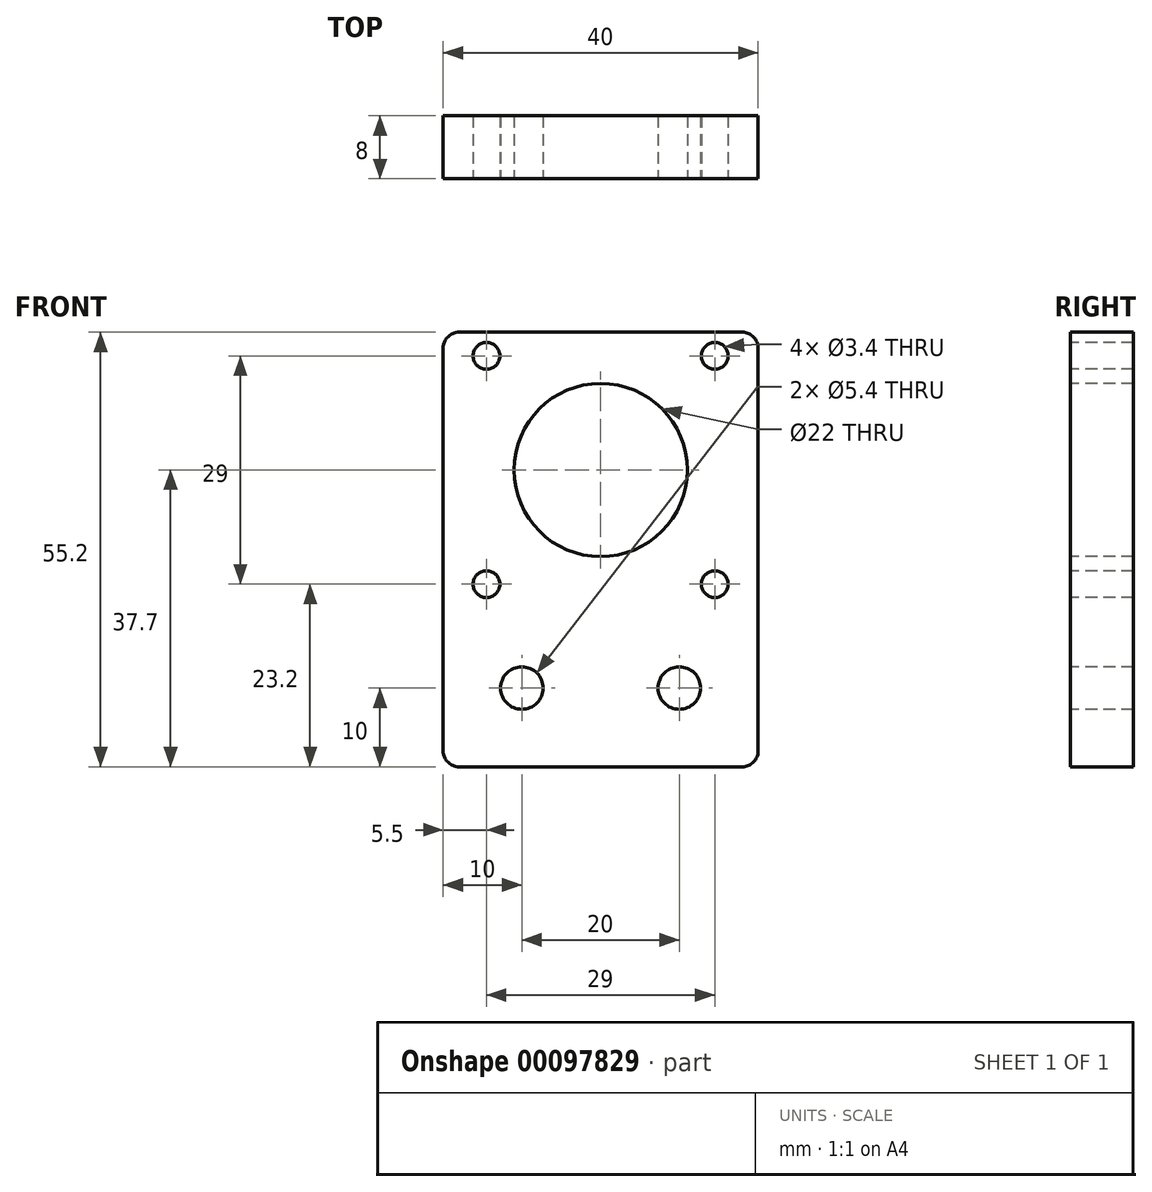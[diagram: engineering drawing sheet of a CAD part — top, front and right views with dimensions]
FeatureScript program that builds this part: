
annotation { "Feature Type Name" : "Feature", "Feature Type Description" : "" }
export const myFeature = defineFeature(function(context is Context, id is Id, definition is map)
    precondition{}
    {
        {
            var Q0;
            Q0=qCreatedBy(makeId("Front.planeOp"),FACE);
            var sketch = newSketch(context, id + "F0", { "sketchPlane" : qUnion([Q0])});
            skLineSegment(sketch, "E0.bottom", {"start": v(20, -17.5) * mm, "end": v(-20, -17.5) * mm, "construction": true});
            skLineSegment(sketch, "E0.top", {"start": v(20, 17.5) * mm, "end": v(-20, 17.5) * mm, "construction": true});
            skLineSegment(sketch, "E0.left", {"start": v(20, -17.5) * mm, "end": v(20, 17.5) * mm, "construction": true});
            skLineSegment(sketch, "E0.right", {"start": v(-20, -17.5) * mm, "end": v(-20, 17.5) * mm, "construction": true});
            skPoint(sketch, "E0.middle", {"position": v(0, 0) * mm});
            skLineSegment(sketch, "E1.bottom", {"start": v(14.5, -14.5) * mm, "end": v(-14.5, -14.5) * mm, "construction": true});
            skLineSegment(sketch, "E1.top", {"start": v(14.5, 14.5) * mm, "end": v(-14.5, 14.5) * mm, "construction": true});
            skLineSegment(sketch, "E1.left", {"start": v(14.5, -14.5) * mm, "end": v(14.5, 14.5) * mm, "construction": true});
            skLineSegment(sketch, "E1.right", {"start": v(-14.5, -14.5) * mm, "end": v(-14.5, 14.5) * mm, "construction": true});
            skCircle(sketch, "E2", {"center": v(-14.5, 14.5) * mm, "radius": 1.7 * mm});
            skCircle(sketch, "E3", {"center": v(14.5, 14.5) * mm, "radius": 1.7 * mm});
            skCircle(sketch, "E4", {"center": v(14.5, -14.5) * mm, "radius": 1.7 * mm});
            skCircle(sketch, "E5", {"center": v(-14.5, -14.5) * mm, "radius": 1.7 * mm});
            skCircle(sketch, "E6", {"center": v(0, 0) * mm, "radius": 4 * mm, "construction": true});
            skCircle(sketch, "E7", {"center": v(0, 0) * mm, "radius": 10 * mm, "construction": true});
            skLineSegment(sketch, "E8", {"start": v(20, -37.7) * mm, "end": v(-20, -37.7) * mm, "construction": true});
            skLineSegment(sketch, "E9", {"start": v(-20, 15.5) * mm, "end": v(-20, -35.7) * mm});
            skLineSegment(sketch, "E10", {"start": v(-18, 17.5) * mm, "end": v(18, 17.5) * mm});
            skLineSegment(sketch, "E11", {"start": v(20, 15.5) * mm, "end": v(20, -35.7) * mm});
            skLineSegment(sketch, "E12", {"start": v(18, -37.7) * mm, "end": v(-18, -37.7) * mm});
            skLineSegment(sketch, "E13", {"start": v(20, -27.7) * mm, "end": v(-20, -27.7) * mm, "construction": true});
            skPoint(sketch, "E14", {"position": v(0, -27.7) * mm});
            skLineSegment(sketch, "E15", {"start": v(0, -27.7) * mm, "end": v(-20, -27.7) * mm, "construction": true});
            skPoint(sketch, "E16", {"position": v(-10, -27.7) * mm});
            skLineSegment(sketch, "E17", {"start": v(0, -27.7) * mm, "end": v(20, -27.7) * mm, "construction": true});
            skPoint(sketch, "E18", {"position": v(10, -27.7) * mm});
            skCircle(sketch, "E19", {"center": v(-10, -27.7) * mm, "radius": 2.7 * mm});
            skCircle(sketch, "E20", {"center": v(10, -27.7) * mm, "radius": 2.7 * mm});
            skPoint(sketch, "E21.visualSharp", {"position": v(-20, 17.5) * mm});
            skArc(sketch, "E21.filletArc", {"start": v(-18, 17.5) * mm, "mid": v(-19.41, 16.91) * mm, "end": v(-20, 15.5) * mm});
            skPoint(sketch, "E22.visualSharp", {"position": v(20, 17.5) * mm});
            skArc(sketch, "E22.filletArc", {"start": v(20, 15.5) * mm, "mid": v(19.41, 16.91) * mm, "end": v(18, 17.5) * mm});
            skPoint(sketch, "E23.visualSharp", {"position": v(20, -37.7) * mm});
            skArc(sketch, "E23.filletArc", {"start": v(18, -37.7) * mm, "mid": v(19.41, -37.11) * mm, "end": v(20, -35.7) * mm});
            skPoint(sketch, "E24.visualSharp", {"position": v(-20, -37.7) * mm});
            skArc(sketch, "E24.filletArc", {"start": v(-20, -35.7) * mm, "mid": v(-19.41, -37.11) * mm, "end": v(-18, -37.7) * mm});
            skCircle(sketch, "E25", {"center": v(0, 0) * mm, "radius": 11 * mm});
            skSolve(sketch);
        }
        {
            var Q0;
            Q0 = qSketchRegion(id + "F0", true);
            extrude(context, id + "F1", {"entities" : qUnion([Q0]), "oppositeDirection" : true, "depth" : 8 * mm});
        }
    });
